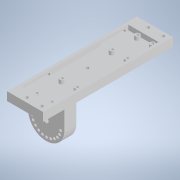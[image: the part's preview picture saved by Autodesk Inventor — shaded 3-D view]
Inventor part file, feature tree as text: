
AUTODESK INVENTOR PART (.ipt)
format: ipt  version: 2021 (Build 250183000, 183)  size: 302,080 bytes
history: native  units: mm
features: extrude x12, sketch x10, reference x4, other x3, projected_geometry x1
ambient origin geometry x8: Origin, YZ Plane, XZ Plane, XY Plane, X Axis, Y Axis, Z Axis, Center Point
bodies: Solid1 (feature_tree)
feature tree (30):
  sketch  "Sketch1"  dims[d19=3.0mm d20=0.0mm d21=4.0mm]
  extrude  "Extrusion1"  Depth=4.0mm
  extrude  "Extrusion2"  Depth=4.0mm
  extrude  "Extrusion3"  Depth=4.0mm
  extrude  "Extrusion4"  Depth=4.0mm
  extrude  "Extrusion5"  Depth=3.0mm TaperAngle=0.0deg
  extrude  "Extrusion6"  Depth=2.0mm
  extrude  "Extrusion7"  Depth=4.0mm TaperAngle=0.0deg
  extrude  "Extrusion8"  Depth=5.0mm
  extrude  "Extrusion9"  Depth=10.0mm TaperAngle=0.0deg
  sketch  "Sketch9"  dims[d37=30.0mm d38=5.0mm]
  extrude  "Extrusion10"  Depth=3.0mm
  extrude  "Extrusion11"  Depth=10.0mm
  extrude  "Extrusion12"  Depth=10.0mm TaperAngle=180.0deg
  sketch  "Sketch2"  dims[d22=4.0mm d23=4.0mm]
  sketch  "Sketch3"  dims[d24=4.0mm d25=4.0mm]
  sketch  "Sketch5"  dims[d26=4.0mm d27=4.0mm]
  sketch  "Sketch6"  dims[d28=4.0mm d29=3.0mm d30=0.0mm]
  sketch  "Sketch7"  dims[d31=4.0mm d32=0.0mm d33=2.0mm]
  sketch  "Sketch8"  dims[d34=5.0mm d35=4.0mm d36=0.0mm]
  projected_geometry  "Projected Loop1"
  reference  "Reference1"
  reference  "Reference2"
  reference  "Reference3"
  reference  "Reference4"
  sketch  "Sketch10"  dims[d39=10.0mm d40=30.0mm d41=0.0mm]
  sketch  "Sketch11"  dims[d42=4.0mm d43=0.0mm d46=3.0mm d47=2.2mm d48=120.0mm d50=180.0deg d52=4.0mm d53=0.0mm d54=4.0mm d55=4.0mm d56=0.0mm d57=0.5mm d58=0.5mm d59=0.5mm d60=0.5mm d61=10.0mm d62=0.0mm d63=10.0mm d64=0.0mm d65=3.0mm d66=0.0mm d67=7.0mm d69=2.9mm d70=2.9mm d71=7.0mm d72=2.9mm d73=2.9mm d74=10.0mm d75=0.0mm]
  parser-record x1  (decoder bookkeeping rows leaked as tree rows — omitted from the tree; the rows remain in map.json)
  other  "assembly.iam"
  other  "pi_cam_stereo_case_cover:1"
note: 1 file-system path scrubbed to <path> (originals preserved in map.json)
